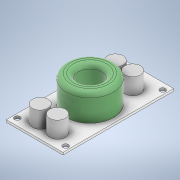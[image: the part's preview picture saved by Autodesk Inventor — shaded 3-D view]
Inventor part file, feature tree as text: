
AUTODESK INVENTOR PART (.ipt)
format: ipt  version: 2020 (Build 240168000, 168)  size: 211,968 bytes
history: native  units: mm
features: extrude x3, sketch x3, other x2, fillet x1
ambient origin geometry x8: Origin, YZ Plane, XZ Plane, XY Plane, X Axis, Y Axis, Z Axis, Center Point
bodies: Body1 (feature_tree)
feature tree (9):
  other  "Твердое тело1"
  extrude  "Выдавливание1"  Depth=36.0mm
  extrude  "Выдавливание2"  Depth=70.3mm
  extrude  "Выдавливание3"  Depth=30.75mm
  other  "РабПлоскость1"
  fillet  "Сопряжение1"  Radius=61.7mm
  sketch  "Эскиз1"
  sketch  "Эскиз2"
  sketch  "Эскиз4"
